# Revit family: Haworth_Cappellini_Bong_Table_AP_PRELIMINARY
name_source: partatom
category: Furniture
revit_build: Autodesk Revit 2018 (Build: 20170223_1515(x64)
units: mm (PartAtom-declared; Revit-internal decimal feet)

## family parameters
Always vertical = Yes
Cut with Voids When Loaded = No
OmniClass Number = 23.40.20.00
OmniClass Title = General Furniture and Specialties
Room Calculation Point = No
Shared = No
Work Plane-Based = No

## types (1)
- Bong table
    Actual Height = 400 mm  [stored 1.31234 ft]
    Assembly Code = E2020200
    Description = Haworth - Cappellini - Bong - Service Table
    Manufacturer = Haworth
    Model = BG_1
    Radius = 240 mm  [stored 0.787402 ft]
    Revision = 4
    Size = Verify Final Dim. w/ Haworth
    URL = https://www.haworth.com
    URL - Product = https://www.haworth.com
    Warranty = http://www.haworth.com

note: [stored X ft] marks values corroborated as IEEE doubles in the binary element streams (Revit-internal decimal feet)

## geometry (parser evidence)
native form markers: Sweep x2
no freeform markers — native parametric forms only
